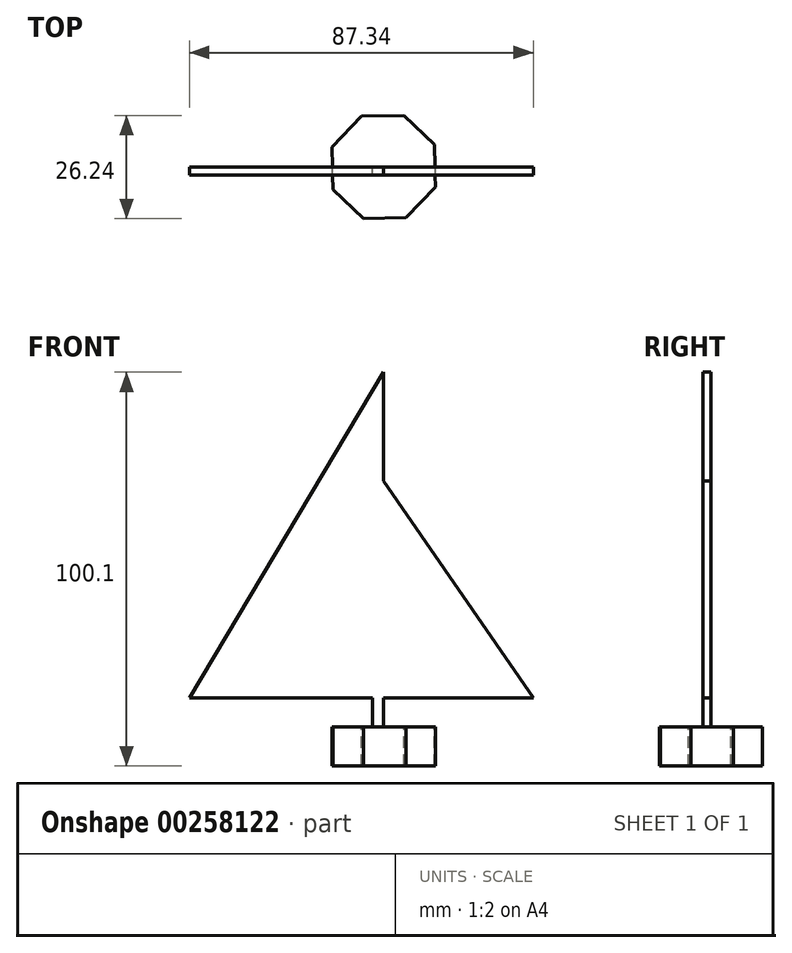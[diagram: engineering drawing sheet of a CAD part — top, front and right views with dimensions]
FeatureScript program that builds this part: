
annotation { "Feature Type Name" : "Feature", "Feature Type Description" : "" }
export const myFeature = defineFeature(function(context is Context, id is Id, definition is map)
    precondition{}
    {
        {
            var Q0;
            Q0=qCreatedBy(makeId("Top.planeOp"),FACE);
            var sketch = newSketch(context, id + "F0", { "sketchPlane" : qUnion([Q0])});
            skCircle(sketch, "E0.cCircle", {"center": v(0, 0) * mm, "radius": 13 * mm, "construction": true});
            skLineSegment(sketch, "E0.0", {"start": v(-13.12, 5.09) * mm, "end": v(-5.68, 12.88) * mm});
            skLineSegment(sketch, "E0.1", {"start": v(-5.68, 12.88) * mm, "end": v(5.09, 13.12) * mm});
            skLineSegment(sketch, "E0.2", {"start": v(5.09, 13.12) * mm, "end": v(12.88, 5.68) * mm});
            skLineSegment(sketch, "E0.3", {"start": v(12.88, 5.68) * mm, "end": v(13.12, -5.09) * mm});
            skLineSegment(sketch, "E0.4", {"start": v(13.12, -5.09) * mm, "end": v(5.68, -12.88) * mm});
            skLineSegment(sketch, "E0.5", {"start": v(5.68, -12.88) * mm, "end": v(-5.09, -13.12) * mm});
            skLineSegment(sketch, "E0.6", {"start": v(-5.09, -13.12) * mm, "end": v(-12.88, -5.68) * mm});
            skLineSegment(sketch, "E0.7", {"start": v(-12.88, -5.68) * mm, "end": v(-13.12, 5.09) * mm});
            skPoint(sketch, "E0.0.midPoint", {"position": v(-9.4, 8.98) * mm});
            skSolve(sketch);
        }
        {
            var Q0;
            Q0=makeQuery(id+"F0.imprint","IMPRINT",FACE,{"disambiguationData":[TD([[makeQuery(id+"F0.imprint","IMPRINT",EDGE,{"derivedFrom":sQuery(id+"F0.wireOp",EDGE,"E0.0")}),-1.0]])]});
            extrude(context, id + "F1", {"entities" : qUnion([Q0]), "oppositeDirection" : true, "depth" : 10 * mm});
        }
        {
            var Q0;
            Q0=qCreatedBy(makeId("Front.planeOp"),FACE);
            var sketch = newSketch(context, id + "F2", { "sketchPlane" : qUnion([Q0])});
            skLineSegment(sketch, "E1", {"start": v(0, 0) * mm, "end": v(0, 14.56) * mm});
            skLineSegment(sketch, "E2", {"start": v(-31.36, 14.56) * mm, "end": v(0, 55.32) * mm});
            skLineSegment(sketch, "E3", {"start": v(0, 55.32) * mm, "end": v(0, 42.57) * mm});
            skLineSegment(sketch, "E4", {"start": v(-31.36, 14.56) * mm, "end": v(-5.62, 14.56) * mm});
            skLineSegment(sketch, "E5", {"start": v(-5.62, 14.56) * mm, "end": v(-2.8, 7.28) * mm});
            skLineSegment(sketch, "E6", {"start": v(0, 42.57) * mm, "end": v(0, 55.32) * mm});
            skLineSegment(sketch, "E7", {"start": v(0, 0) * mm, "end": v(-2.8, 0) * mm});
            skLineSegment(sketch, "E8", {"start": v(-2.8, 0) * mm, "end": v(-2.8, 7.28) * mm});
            skPoint(sketch, "E8.endSnap0", {"position": v(-2.8, 7.28) * mm});
            skLineSegment(sketch, "E9", {"start": v(-2.8, 7.28) * mm, "end": v(-2.8, 7.28) * mm});
            skLineSegment(sketch, "E10", {"start": v(0, 14.56) * mm, "end": v(20.74, 14.56) * mm});
            skLineSegment(sketch, "E11", {"start": v(20.74, 14.56) * mm, "end": v(0, 42.57) * mm});
            skLineSegment(sketch, "E12", {"start": v(-2.8, 7.28) * mm, "end": v(-49.32, 7.28) * mm});
            skLineSegment(sketch, "E13", {"start": v(-49.32, 7.28) * mm, "end": v(0, 90.1) * mm});
            skLineSegment(sketch, "E14", {"start": v(0, 90.1) * mm, "end": v(0, 62.5) * mm});
            skLineSegment(sketch, "E15", {"start": v(0, 62.5) * mm, "end": v(38.02, 7.28) * mm});
            skLineSegment(sketch, "E16", {"start": v(38.02, 7.28) * mm, "end": v(0, 7.28) * mm});
            skSolve(sketch);
        }
        {
            var Q0;
            Q0=makeQuery(id+"F2.imprint","IMPRINT",FACE,{"disambiguationData":[TD([[makeQuery(id+"F2.imprint","IMPRINT",EDGE,{"derivedFrom":sQuery(id+"F2.wireOp",EDGE,"E1")}),1.0]])]});
            var Q1;
            Q1=makeQuery(id+"F2.imprint","IMPRINT",FACE,{"disambiguationData":[TD([[makeQuery(id+"F2.imprint","IMPRINT",EDGE,{"derivedFrom":sQuery(id+"F2.wireOp",EDGE,"E2")}),1.0]])]});
            extrude(context, id + "F3", {"entities" : qUnion([Q0, Q1]), "depth" : 2 * mm});
        }
    });
